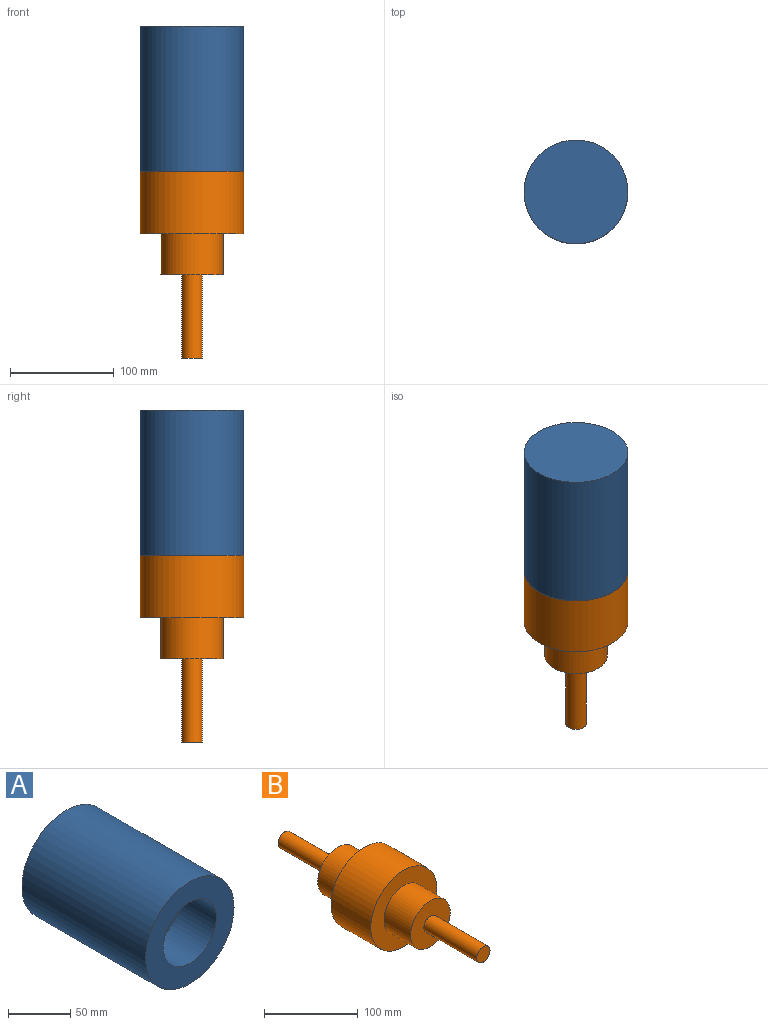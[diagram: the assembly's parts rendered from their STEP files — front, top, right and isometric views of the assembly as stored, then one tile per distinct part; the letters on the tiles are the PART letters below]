
ASSEMBLY  parts=2 mates=1
PART A: 7 faces, bbox 100x140x100 mm
  f0: cylinder r=50mm len=140mm, axis (0,1,0), area 43982.3mm2, adj f1,f2
  f1: plane 100x100mm, normal (0,-1,0), area 5026.5mm2, adj f0,f3
  f2: plane 100x100mm, normal (0,1,0), area 7854mm2, adj f0
  f3: cylinder r=30mm len=60mm, axis (0,-1,0), area 7539.8mm2, adj f1,f4
  f4: plane 60x60mm, normal (0,-1,0), area 2513.3mm2, adj f3,f5
  f5: cylinder r=10mm len=80mm, axis (0,-1,0), area 5026.5mm2, adj f4,f6
  f6: plane 20x20mm, normal (0,-1,0), area 314.2mm2, adj f5
PART B: 11 faces, bbox 100x300x100 mm
  f0: cylinder r=50mm len=100mm, axis (0,1,0), area 18849.6mm2, adj f1,f2
  f1: plane 100x100mm, normal (0,-1,0), area 5026.5mm2, adj f0,f3
  f2: plane 100x100mm, normal (0,1,0), area 5026.5mm2, adj f0,f7
  f3: cylinder r=30mm len=60mm, axis (0,1,0), area 7539.8mm2, adj f1,f4
  f4: plane 60x60mm, normal (0,-1,0), area 2513.3mm2, adj f3,f5
  f5: cylinder r=10mm len=80mm, axis (0,1,0), area 5026.5mm2, adj f4,f6
  f6: plane 20x20mm, normal (0,-1,0), area 314.2mm2, adj f5
  f7: cylinder r=30mm len=60mm, axis (0,-1,0), area 7539.8mm2, adj f2,f8
  f8: plane 60x60mm, normal (0,1,0), area 2513.3mm2, adj f7,f9
  f9: cylinder r=10mm len=80mm, axis (0,-1,0), area 5026.5mm2, adj f8,f10
  f10: plane 20x20mm, normal (0,1,0), area 314.2mm2, adj f9
PLACE A rot(axis=(1,0,0),90deg) t=(0,0,140)mm
PLACE B rot(axis=(1,0,0),90deg) t=(0,0,0)mm
MATE fastened A.f0 <-> B.f0  axis (0,0,1) through (0,0,0)mm
